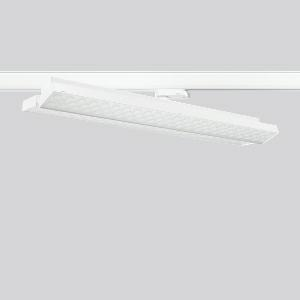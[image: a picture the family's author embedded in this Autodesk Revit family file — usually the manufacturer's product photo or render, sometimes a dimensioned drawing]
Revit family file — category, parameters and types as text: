
# Revit family: tx-move_742163_002_1_5258
name_source: partatom
category: Lighting Fixtures
units: mm (PartAtom-declared; Revit-internal decimal feet)

## family parameters
Cut with Voids When Loaded = No
Host = Face
Light Source = No
Part Type = Normal
Room Calculation Point = No
Round Connector Dimension = Use Diameter
Shared = No

## types (1)
- MultiLumen 1 (1 x LED Modul 840, 2950 lm, 4000)
    Apparent Load = 41 VA
    CIE Flux Codes = 65 90 98 100 100
    Color Rendering = 80
    Color Temperature = 4000
    Default Elevation = 1800 mm
    Description = Series: TX-MOVE
Multifunctional surface-mounted spotlight for area lighting. Very flat design. Housing: sheet steel, powder-coated. Rotation range: 356°. Swivel range: 90°. Consistent alignment possible with visible tilt scale. High-efficiency LED units with optimum light control thanks to clear plastic (PC) lens optics. Spezielle Mikrostrukturen reduzieren Gelbsaum. Asymmetrical light distribution. With multi adaptor for 3-circuit tracks 230 V. Suitable for Track on ceiling. MultiLumen: Luminous flux adjustable in 3 steps. Factory setting is the highest luminous flux. Environmentally friendly and resource-saving due to replaceable and recyclable components. 
Colour: traffic white, matt (RAL 9016)
Length: 570 mm
Width: 119 mm
Height: 92 mm
Lamp: LED
Socket: without socket
Colour temperature: 4000K
Colour rendering index (CRI): 80
System power: 41 W
Rated luminous flux: 5900 lm
Luminous efficiency: 144 lm/W
System power 2: 57 W
Rated luminous flux 2: 8000 lm
Luminous efficiency 2: 140 lm/W
System power 3: 73 W
Rated luminous flux 3: 9750 lm
Luminous efficiency 3: 134 lm/W
Control gear: Regulated power supply
Protection class: I
Type of protection: IP 20
    Height = 75 mm
    Lamp = 1 x LED Modul 840
    Lamp Light Flux = 2950 lm
    Lamp count = 1
    Length = 569 mm
    Lifetime = 50000 h
    Luminous efficacy = 144 lm/W
    Manufacturer = RZB
    ModVariant = No
    Model = 742163.002.1
    Mounting Place = Ceiling
    Mounting Type = Surface mounted
    Number of Poles = 1
    OnlyDefault = Yes
    Power Factor = 1
    Product Name = TX-MOVE
    Product group = Track mounted projectors
    ProductGroupID = 301
    Protection Class = Protection class I
    Protection Degree = IP 20
    RLX_Detail_Level = 1
    RLX_Emergency_Light_Flux = 0 lm
    RLX_Emergency_Type = 0
    RLX_Emergency_Type_DB = No
    RlxData = <blob elided: 51753 chars, md5=8326012b>
    Socket = socket
    Standby Power = 0 W
    System Light Flux = 5900 lm
    System Power = 41 W
    Type Comments = MultiLumen 1
    Type Image = 742162.002.jpg
    URL = http://relux.com
    VarID = multilumen_1
    Voltage = 0 V
    Weight = 0.00 kg
    Width = 119 mm

## geometry (parser evidence)
native form markers: Blend x4, Sweep x14
no freeform markers — native parametric forms only
